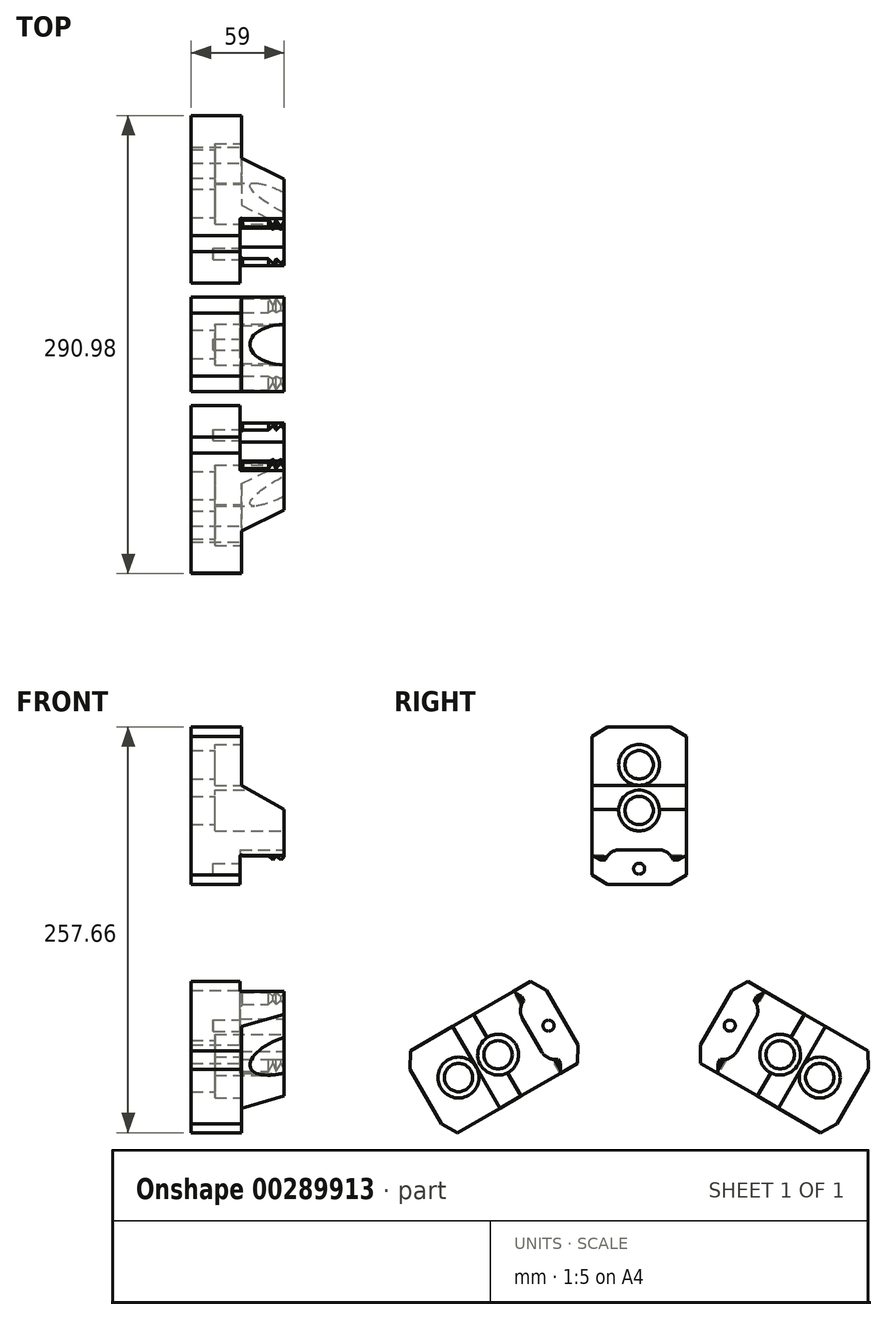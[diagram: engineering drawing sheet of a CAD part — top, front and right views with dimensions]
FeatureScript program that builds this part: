
annotation { "Feature Type Name" : "Feature", "Feature Type Description" : "" }
export const myFeature = defineFeature(function(context is Context, id is Id, definition is map)
    precondition{}
    {
        {
            var Q0;
            Q0=qCreatedBy(makeId("Front.planeOp"),FACE);
            var sketch = newSketch(context, id + "F0", { "sketchPlane" : qUnion([Q0])});
            skLineSegment(sketch, "E0", {"start": v(3, 56.45) * mm, "end": v(3, 156.45) * mm});
            skLineSegment(sketch, "E1", {"start": v(3, 156.45) * mm, "end": v(35, 156.45) * mm});
            skLineSegment(sketch, "E2", {"start": v(35, 156.45) * mm, "end": v(35, 119.45) * mm});
            skLineSegment(sketch, "E3", {"start": v(35, 119.45) * mm, "end": v(62, 104) * mm});
            skLineSegment(sketch, "E4", {"start": v(62, 104) * mm, "end": v(62, 74) * mm});
            skLineSegment(sketch, "E5", {"start": v(3, 56.45) * mm, "end": v(34, 56.45) * mm});
            skLineSegment(sketch, "E6", {"start": v(34, 56.45) * mm, "end": v(34, 74.45) * mm});
            skLineSegment(sketch, "E7", {"start": v(52, 74.45) * mm, "end": v(55, 72) * mm});
            skLineSegment(sketch, "E8", {"start": v(55, 72) * mm, "end": v(57, 74.45) * mm});
            skLineSegment(sketch, "E9", {"start": v(57, 74.45) * mm, "end": v(60, 72) * mm});
            skLineSegment(sketch, "E10", {"start": v(60, 72) * mm, "end": v(62, 74) * mm});
            skArc(sketch, "E11", {"start": v(35.5, 74.45) * mm, "mid": v(34.75, 75.2) * mm, "end": v(34, 74.45) * mm});
            skLineSegment(sketch, "E12.trimOffspring", {"start": v(35.5, 74.45) * mm, "end": v(52, 74.45) * mm});
            skLineSegment(sketch, "E13", {"start": v(0, 0) * mm, "end": v(70.08, 0) * mm, "construction": true});
            skSolve(sketch);
        }
        {
            var Q0;
            Q0=qSketchRegion(id+"F0",true);
            extrude(context, id + "F1", {"entities" : qUnion([Q0]), "endBound" : BoundingType.SYMMETRIC, "depth" : 60 * mm});
        }
        {
            var Q0;
            Q0=makeQuery(id+"F1.opExtrude","SWEPT_FACE",FACE,{"disambiguationData":[OSD([sQuery(id+"F0.wireOp",EDGE,"E2")])]});
            var sketch = newSketch(context, id + "F2", { "sketchPlane" : qUnion([Q0])});
            skLineSegment(sketch, "E14", {"start": v(20, 156.45) * mm, "end": v(30, 150.45) * mm});
            skLineSegment(sketch, "E15", {"start": v(30, 150.45) * mm, "end": v(30, 156.45) * mm});
            skLineSegment(sketch, "E16", {"start": v(30, 156.45) * mm, "end": v(20, 156.45) * mm});
            skLineSegment(sketch, "E17", {"start": v(20, 56.45) * mm, "end": v(30, 62.45) * mm});
            skLineSegment(sketch, "E18", {"start": v(30, 62.45) * mm, "end": v(30, 56.45) * mm});
            skLineSegment(sketch, "E19", {"start": v(30, 56.45) * mm, "end": v(20, 56.45) * mm});
            skLineSegment(sketch, "E20", {"start": v(0, 42.7) * mm, "end": v(0, 168.17) * mm, "construction": true});
            skLineSegment(sketch, "E21.MirrorCS", {"start": v(-20, 156.45) * mm, "end": v(-30, 150.45) * mm});
            skLineSegment(sketch, "E22.MirrorCS", {"start": v(-30, 156.45) * mm, "end": v(-20, 156.45) * mm});
            skLineSegment(sketch, "E23.MirrorCS", {"start": v(-30, 150.45) * mm, "end": v(-30, 156.45) * mm});
            skLineSegment(sketch, "E24.MirrorCS", {"start": v(-20, 56.45) * mm, "end": v(-30, 62.45) * mm});
            skLineSegment(sketch, "E25.MirrorCS", {"start": v(-30, 62.45) * mm, "end": v(-30, 56.45) * mm});
            skLineSegment(sketch, "E26.MirrorCS", {"start": v(-30, 56.45) * mm, "end": v(-20, 56.45) * mm});
            skSolve(sketch);
        }
        {
            var Q0;
            Q0=makeQuery(id+"F2.imprint","IMPRINT",FACE,{"disambiguationData":[TD([[makeQuery(id+"F2.imprint","IMPRINT",EDGE,{"derivedFrom":sQuery(id+"F2.wireOp",EDGE,"E21.MirrorCS")}),-1.0]])]});
            var Q1;
            Q1=makeQuery(id+"F2.imprint","IMPRINT",FACE,{"disambiguationData":[TD([[makeQuery(id+"F2.imprint","IMPRINT",EDGE,{"derivedFrom":sQuery(id+"F2.wireOp",EDGE,"E14")}),1.0]])]});
            var Q2;
            Q2=makeQuery(id+"F2.imprint","IMPRINT",FACE,{"disambiguationData":[TD([[makeQuery(id+"F2.imprint","IMPRINT",EDGE,{"derivedFrom":sQuery(id+"F2.wireOp",EDGE,"E17")}),-1.0]])]});
            var Q3;
            Q3=makeQuery(id+"F2.imprint","IMPRINT",FACE,{"disambiguationData":[TD([[makeQuery(id+"F2.imprint","IMPRINT",EDGE,{"derivedFrom":sQuery(id+"F2.wireOp",EDGE,"E24.MirrorCS")}),1.0]])]});
            var Q4;
            Q4=makeQuery(id+"F1.opExtrude","SWEPT_FACE",FACE,{"disambiguationData":[OSD([sQuery(id+"F0.wireOp",EDGE,"E0")])]});
            extrude(context, id + "F3", {"entities" : qUnion([Q0, Q1, Q2, Q3]), "operationType" : NewBodyOperationType.REMOVE, "endBound" : BoundingType.UP_TO_SURFACE, "oppositeDirection" : true, "endBoundEntityFace" : qUnion([Q4]), "depth" : 25 * mm});
        }
        {
            var Q0;
            Q0=makeQuery(id+"F1.opExtrude","SWEPT_FACE",FACE,{"disambiguationData":[OSD([sQuery(id+"F0.wireOp",EDGE,"E4")])]});
            var sketch = newSketch(context, id + "F4", { "sketchPlane" : qUnion([Q0])});
            skLineSegment(sketch, "E27", {"start": v(30, 75) * mm, "end": v(24.5, 72) * mm});
            skLineSegment(sketch, "E28", {"start": v(24.5, 72) * mm, "end": v(30, 72) * mm});
            skLineSegment(sketch, "E29", {"start": v(30, 72) * mm, "end": v(30, 75) * mm});
            skLineSegment(sketch, "E30", {"start": v(0, 67.05) * mm, "end": v(0, 113.15) * mm, "construction": true});
            skPoint(sketch, "E30.endSnap0", {"position": v(0, 104) * mm});
            skLineSegment(sketch, "E31.MirrorCS", {"start": v(-30, 75) * mm, "end": v(-24.5, 72) * mm});
            skLineSegment(sketch, "E32.MirrorCS", {"start": v(-30, 72) * mm, "end": v(-30, 75) * mm});
            skLineSegment(sketch, "E33.MirrorCS", {"start": v(-24.5, 72) * mm, "end": v(-30, 72) * mm});
            skSolve(sketch);
        }
        {
            var Q0;
            {var subQ0=sQuery(id+"F4.wireOp",EDGE,"E33.MirrorCS");Q0=makeQuery(id+"F4.imprint","IMPRINT",FACE,{"disambiguationData":[TD([[makeQuery(id+"F4.imprint","IMPRINT",EDGE,{"derivedFrom":subQ0}),-1.0]])]});}
            var Q1;
            {var subQ0=sQuery(id+"F4.wireOp",EDGE,"E32.MirrorCS");var subQ1=sQuery(id+"F4.wireOp",EDGE,"E31.MirrorCS");var subQ2=sQuery(id+"F0.wireOp",EDGE,"E4");var subQ3=makeQuery(id+"F4.imprint","INTERSECT",VERTEX,{"derivedFrom":[makeQuery(id+"F1.opExtrude","CAP_EDGE",EDGE,{"disambiguationData":[OSD([subQ2])],"isStart":false}),subQ1,subQ0]});Q1=makeQuery(id+"F4.imprint","IMPRINT",FACE,{"disambiguationData":[TD([[makeQuery(id+"F4.imprint","IMPRINT",EDGE,{"disambiguationData":[TD([[subQ3,-1.0]])],"derivedFrom":subQ1}),-1.0]])]});}
            var Q2;
            {var subQ0=sQuery(id+"F4.wireOp",EDGE,"E29");var subQ1=sQuery(id+"F4.wireOp",EDGE,"E27");var subQ2=sQuery(id+"F0.wireOp",EDGE,"E4");var subQ3=makeQuery(id+"F4.imprint","INTERSECT",VERTEX,{"derivedFrom":[makeQuery(id+"F1.opExtrude","CAP_EDGE",EDGE,{"disambiguationData":[OSD([subQ2])],"isStart":true}),subQ1,subQ0]});Q2=makeQuery(id+"F4.imprint","IMPRINT",FACE,{"disambiguationData":[TD([[makeQuery(id+"F4.imprint","IMPRINT",EDGE,{"disambiguationData":[TD([[subQ3,-1.0]])],"derivedFrom":subQ1}),1.0]])]});}
            var Q3;
            {var subQ0=sQuery(id+"F4.wireOp",EDGE,"E28");Q3=makeQuery(id+"F4.imprint","IMPRINT",FACE,{"disambiguationData":[TD([[makeQuery(id+"F4.imprint","IMPRINT",EDGE,{"derivedFrom":subQ0}),1.0]])]});}
            var Q4;
            Q4=makeQuery(id+"F1.opExtrude","SWEPT_FACE",FACE,{"disambiguationData":[OSD([sQuery(id+"F0.wireOp",EDGE,"E6")])]});
            extrude(context, id + "F5", {"entities" : qUnion([Q0, Q1, Q2, Q3]), "operationType" : NewBodyOperationType.REMOVE, "endBound" : BoundingType.UP_TO_SURFACE, "oppositeDirection" : true, "endBoundEntityFace" : qUnion([Q4]), "depth" : 27.7 * mm});
        }
        {
            var Q0;
            Q0=makeQuery(id+"F1.opExtrude","SWEPT_FACE",FACE,{"disambiguationData":[OSD([sQuery(id+"F0.wireOp",EDGE,"E4")])]});
            var sketch = newSketch(context, id + "F6", { "sketchPlane" : qUnion([Q0])});
            skLineSegment(sketch, "E34", {"start": v(0, 70.5) * mm, "end": v(0, 96.88) * mm, "construction": true});
            skPoint(sketch, "E34.startSnap0", {"position": v(0, 74) * mm});
            skLineSegment(sketch, "E35", {"start": v(12.26, 78.5) * mm, "end": v(0, 78.5) * mm});
            skLineSegment(sketch, "E36", {"start": v(21.5, 72) * mm, "end": v(0, 72) * mm});
            skPoint(sketch, "E37", {"position": v(12, 78.5) * mm});
            skArc(sketch, "E38", {"start": v(21.5, 72) * mm, "mid": v(17.78, 76.75) * mm, "end": v(12, 78.5) * mm});
            skPoint(sketch, "E39.end.orphan", {"position": v(21.5, 78.5) * mm});
            skLineSegment(sketch, "E40.MirrorCS", {"start": v(-12.26, 78.5) * mm, "end": v(0, 78.5) * mm});
            skArc(sketch, "E41.MirrorCS", {"start": v(-21.5, 72) * mm, "mid": v(-17.78, 76.75) * mm, "end": v(-12, 78.5) * mm});
            skLineSegment(sketch, "E42.MirrorCS", {"start": v(-21.5, 72) * mm, "end": v(0, 72) * mm});
            skSolve(sketch);
        }
        {
            var Q0;
            Q0=qSketchRegion(id+"F6",true);
            var Q1;
            Q1=makeQuery(id+"F5.boolean.opBoolean","MERGE",FACE,{"derivedFrom":[makeQuery(id+"F1.opExtrude","SWEPT_FACE",FACE,{"disambiguationData":[OSD([sQuery(id+"F0.wireOp",EDGE,"E6")])]})],"fromTools":[makeQuery(id+"F5.opExtrude","CAP_FACE",FACE,{"disambiguationData":[OSD([sQuery(id+"F4.wireOp",EDGE,"E27"),sQuery(id+"F4.wireOp",EDGE,"E28"),sQuery(id+"F4.wireOp",EDGE,"E29")])],"isStart":false}),makeQuery(id+"F5.opExtrude","CAP_FACE",FACE,{"disambiguationData":[OSD([sQuery(id+"F4.wireOp",EDGE,"E31.MirrorCS"),sQuery(id+"F4.wireOp",EDGE,"E32.MirrorCS"),sQuery(id+"F4.wireOp",EDGE,"E33.MirrorCS")])],"isStart":false})]});
            extrude(context, id + "F7", {"entities" : qUnion([Q0]), "operationType" : NewBodyOperationType.REMOVE, "endBound" : BoundingType.UP_TO_SURFACE, "oppositeDirection" : true, "endBoundEntityFace" : qUnion([Q1]), "depth" : 25 * mm});
        }
        {
            var Q0;
            Q0=makeQuery(id+"F7.boolean.opBoolean","MERGE",FACE,{"derivedFrom":[makeQuery(id+"F5.boolean.opBoolean","MERGE",FACE,{"derivedFrom":[makeQuery(id+"F1.opExtrude","SWEPT_FACE",FACE,{"disambiguationData":[OSD([sQuery(id+"F0.wireOp",EDGE,"E6")])]})],"fromTools":[makeQuery(id+"F5.opExtrude","CAP_FACE",FACE,{"disambiguationData":[OSD([sQuery(id+"F4.wireOp",EDGE,"E27"),sQuery(id+"F4.wireOp",EDGE,"E28"),sQuery(id+"F4.wireOp",EDGE,"E29")])],"isStart":false}),makeQuery(id+"F5.opExtrude","CAP_FACE",FACE,{"disambiguationData":[OSD([sQuery(id+"F4.wireOp",EDGE,"E31.MirrorCS"),sQuery(id+"F4.wireOp",EDGE,"E32.MirrorCS"),sQuery(id+"F4.wireOp",EDGE,"E33.MirrorCS")])],"isStart":false})]})],"fromTools":[makeQuery(id+"F7.opExtrude","CAP_FACE",FACE,{"disambiguationData":[OSD([sQuery(id+"F6.wireOp",EDGE,"E35"),sQuery(id+"F6.wireOp",EDGE,"E36"),sQuery(id+"F6.wireOp",EDGE,"E38"),sQuery(id+"F6.wireOp",EDGE,"E40.MirrorCS"),sQuery(id+"F6.wireOp",EDGE,"E41.MirrorCS"),sQuery(id+"F6.wireOp",EDGE,"E42.MirrorCS")])],"isStart":false})]});
            var sketch = newSketch(context, id + "F8", { "sketchPlane" : qUnion([Q0])});
            skCircle(sketch, "E43.cCircle", {"center": v(0, 66.45) * mm, "radius": 6.5 * mm, "construction": true});
            skLineSegment(sketch, "E43.0", {"start": v(7.5, 66.45) * mm, "end": v(3.75, 59.95) * mm});
            skLineSegment(sketch, "E43.1", {"start": v(3.75, 59.95) * mm, "end": v(-3.75, 59.95) * mm});
            skLineSegment(sketch, "E43.2", {"start": v(-3.75, 59.95) * mm, "end": v(-7.5, 66.45) * mm});
            skLineSegment(sketch, "E43.3", {"start": v(-7.5, 66.45) * mm, "end": v(-3.75, 72.95) * mm});
            skLineSegment(sketch, "E43.4", {"start": v(-3.75, 72.95) * mm, "end": v(3.75, 72.95) * mm});
            skLineSegment(sketch, "E43.5", {"start": v(3.75, 72.95) * mm, "end": v(7.5, 66.45) * mm});
            skPoint(sketch, "E43.0.midPoint", {"position": v(5.63, 63.2) * mm});
            skCircle(sketch, "E44", {"center": v(0, 66.45) * mm, "radius": 3.5 * mm});
            skSolve(sketch);
        }
        {
            var Q0;
            Q0=makeQuery(id+"F8.imprint","IMPRINT",FACE,{"disambiguationData":[TD([[makeQuery(id+"F8.imprint","IMPRINT",EDGE,{"derivedFrom":sQuery(id+"F8.wireOp",EDGE,"E44")}),1.0]])]});
            extrude(context, id + "F9", {"entities" : qUnion([Q0]), "operationType" : NewBodyOperationType.REMOVE, "oppositeDirection" : true, "depth" : 17 * mm});
        }
        {
            var Q0;
            Q0=makeQuery(id+"F1.opExtrude","SWEPT_FACE",FACE,{"disambiguationData":[OSD([sQuery(id+"F0.wireOp",EDGE,"E4")])]});
            var sketch = newSketch(context, id + "F10", { "sketchPlane" : qUnion([Q0])});
            skLineSegment(sketch, "E45", {"start": v(0, 77.6) * mm, "end": v(0, 164.13) * mm, "construction": true});
            skPoint(sketch, "E45.startSnap0", {"position": v(0, 78.5) * mm});
            skCircle(sketch, "E46", {"center": v(0, 132.45) * mm, "radius": 13 * mm});
            skCircle(sketch, "E47", {"center": v(0, 103.45) * mm, "radius": 13 * mm});
            skCircle(sketch, "E48", {"center": v(0, 132.45) * mm, "radius": 9 * mm});
            skCircle(sketch, "E49", {"center": v(0, 103.45) * mm, "radius": 9 * mm});
            skSolve(sketch);
        }
        {
            var Q0;
            Q0=makeQuery(id+"F10.imprint","IMPRINT",FACE,{"disambiguationData":[TD([[makeQuery(id+"F10.imprint","IMPRINT",EDGE,{"derivedFrom":sQuery(id+"F10.wireOp",EDGE,"E48")}),1.0]])]});
            var Q1;
            {var subQ0=sQuery(id+"F10.wireOp",EDGE,"E49");var subQ1=makeQuery(id+"F1.opExtrude","SWEPT_EDGE",EDGE,{"disambiguationData":[OSD([sQuery(id+"F0.wireOp",EDGE,"E3"),sQuery(id+"F0.wireOp",EDGE,"E4")])]});var subQ2=makeQuery(id+"F10.imprint","INTERSECT",VERTEX,{"disambiguationData":[OD(0.0)],"derivedFrom":[subQ1,subQ0]});Q1=makeQuery(id+"F10.imprint","IMPRINT",FACE,{"disambiguationData":[TD([[makeQuery(id+"F10.imprint","IMPRINT",EDGE,{"disambiguationData":[TD([[subQ2,1.0]])],"derivedFrom":subQ0}),1.0]])]});}
            var Q2;
            {var subQ0=sQuery(id+"F10.wireOp",EDGE,"E49");var subQ1=makeQuery(id+"F1.opExtrude","SWEPT_EDGE",EDGE,{"disambiguationData":[OSD([sQuery(id+"F0.wireOp",EDGE,"E3"),sQuery(id+"F0.wireOp",EDGE,"E4")])]});var subQ2=makeQuery(id+"F10.imprint","INTERSECT",VERTEX,{"disambiguationData":[OD(0.0)],"derivedFrom":[subQ1,subQ0]});Q2=makeQuery(id+"F10.imprint","IMPRINT",FACE,{"disambiguationData":[TD([[makeQuery(id+"F10.imprint","IMPRINT",EDGE,{"disambiguationData":[TD([[subQ2,-1.0]])],"derivedFrom":subQ0}),1.0]])]});}
            var Q3;
            Q3=makeQuery(id+"F1.opExtrude","SWEPT_FACE",FACE,{"disambiguationData":[OSD([sQuery(id+"F0.wireOp",EDGE,"E0")])]});
            extrude(context, id + "F11", {"entities" : qUnion([Q0, Q1, Q2]), "operationType" : NewBodyOperationType.REMOVE, "endBound" : BoundingType.UP_TO_SURFACE, "oppositeDirection" : true, "endBoundEntityFace" : qUnion([Q3]), "depth" : 25 * mm});
        }
        {
            var Q0;
            Q0=makeQuery(id+"F10.imprint","IMPRINT",FACE,{"disambiguationData":[TD([[makeQuery(id+"F10.imprint","IMPRINT",EDGE,{"derivedFrom":sQuery(id+"F10.wireOp",EDGE,"E46")}),1.0]])]});
            var Q1;
            {var subQ0=sQuery(id+"F10.wireOp",EDGE,"E47");var subQ1=makeQuery(id+"F1.opExtrude","SWEPT_EDGE",EDGE,{"disambiguationData":[OSD([sQuery(id+"F0.wireOp",EDGE,"E3"),sQuery(id+"F0.wireOp",EDGE,"E4")])]});var subQ2=makeQuery(id+"F10.imprint","INTERSECT",VERTEX,{"disambiguationData":[OD(0.0)],"derivedFrom":[subQ1,subQ0]});Q1=makeQuery(id+"F10.imprint","IMPRINT",FACE,{"disambiguationData":[TD([[makeQuery(id+"F10.imprint","IMPRINT",EDGE,{"disambiguationData":[TD([[subQ2,-1.0]])],"derivedFrom":subQ0}),1.0]])]});}
            var Q2;
            {var subQ0=sQuery(id+"F10.wireOp",EDGE,"E47");var subQ1=makeQuery(id+"F1.opExtrude","SWEPT_EDGE",EDGE,{"disambiguationData":[OSD([sQuery(id+"F0.wireOp",EDGE,"E3"),sQuery(id+"F0.wireOp",EDGE,"E4")])]});var subQ2=makeQuery(id+"F10.imprint","INTERSECT",VERTEX,{"disambiguationData":[OD(0.0)],"derivedFrom":[subQ1,subQ0]});Q2=makeQuery(id+"F10.imprint","IMPRINT",FACE,{"disambiguationData":[TD([[makeQuery(id+"F10.imprint","IMPRINT",EDGE,{"disambiguationData":[TD([[subQ2,1.0]])],"derivedFrom":subQ0}),1.0]])]});}
            extrude(context, id + "F12", {"entities" : qUnion([Q0, Q1, Q2]), "operationType" : NewBodyOperationType.REMOVE, "oppositeDirection" : true, "depth" : 44 * mm});
        }
        {
            var Q0;
            Q0=makeQuery(id+"F1.opExtrude","SWEPT_BODY",BODY,{"disambiguationData":[OSD([sQuery(id+"F0.wireOp",EDGE,"E0"),sQuery(id+"F0.wireOp",EDGE,"E1"),sQuery(id+"F0.wireOp",EDGE,"E2"),sQuery(id+"F0.wireOp",EDGE,"E3"),sQuery(id+"F0.wireOp",EDGE,"E4"),sQuery(id+"F0.wireOp",EDGE,"E5"),sQuery(id+"F0.wireOp",EDGE,"E6"),sQuery(id+"F0.wireOp",EDGE,"E7"),sQuery(id+"F0.wireOp",EDGE,"E8"),sQuery(id+"F0.wireOp",EDGE,"E9"),sQuery(id+"F0.wireOp",EDGE,"E10"),sQuery(id+"F0.wireOp",EDGE,"E11"),sQuery(id+"F0.wireOp",EDGE,"E12.trimOffspring")])]});
            var Q1;
            Q1=sQuery(id+"F0.wireOp",EDGE,"E13");
            circularPattern(context, id + "F13", {"entities" : qUnion([Q0]), "axis" : qUnion([Q1]), "angle" : 360 * degree, "instanceCount" : 3, "equalSpace" : true});
        }
    });
